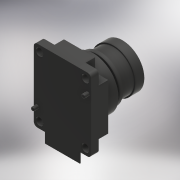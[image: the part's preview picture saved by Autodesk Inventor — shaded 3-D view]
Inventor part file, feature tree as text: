
AUTODESK INVENTOR PART (.ipt)
format: ipt  version: 2017 (Build 210142000, 142)  size: 262,656 bytes
history: native  units: mm
features: sketch x6, extrude x4, projected_geometry x3, fillet x2, revolve x1, hole x1
ambient origin geometry x8: Origin, YZ Plane, XZ Plane, XY Plane, X Axis, Y Axis, Z Axis, Center Point
bodies: Solid1 (feature_tree)
feature tree (17):
  extrude  "Extrusion1"  Depth=19.95mm
  extrude  "Extrusion2"  Depth=3.6mm
  revolve  "Revolution1"  [1 undecoded]
  hole  "Hole1"  [1 undecoded]
  extrude  "Extrusion3"  Depth=16.5mm
  fillet  "Fillet1"  Radius=12.0mm
  fillet  "Fillet2"  Radius=16.5mm
  extrude  "Extrusion4"  Depth=3.7mm
  sketch  "Sketch1"  dims[d0=15.75mm d1=19.95mm]
  sketch  "Sketch2"  dims[d2=4.7mm d3=0.0mm d4=3.6mm]
  projected_geometry  "Projected Loop1"
  sketch  "Sketch3"  dims[d5=3.6mm d6=1.5mm]
  projected_geometry  "Projected Loop2"
  sketch  "Sketch4"  dims[d7=2.6mm d8=0.0mm d9=14.0mm]
  projected_geometry  "Projected Loop3"
  sketch  "Sketch5"  dims[d10=11.3mm d11=12.56mm d12=12.0mm d13=16.5mm]
  sketch  "Sketch6"  dims[d14=2.5mm d15=3.7mm d16=1.0mm d17=1.0mm d18=3.6mm d19=90.0deg d20=6.96mm d21=5.6mm d22=1.8mm d23=12.6mm d24=16.5mm d25=2.0mm d26=6.0mm d27=4.0mm d28=2.0mm d29=90.0deg d30=8.0mm d31=20.594885mm d32=1.0mm d33=1.0mm d34=13.9mm d35=10.0mm d36=1.36mm d37=0.0mm d38=0.3mm d39=1.0mm d40=0.2mm d41=9.6mm d42=2.75mm d43=0.0mm]
note: 2 required parameter values undecoded (feature->parameter linkage not recoverable at this tier; creation-order binding heuristic only, values carry confidence <= 0.55)